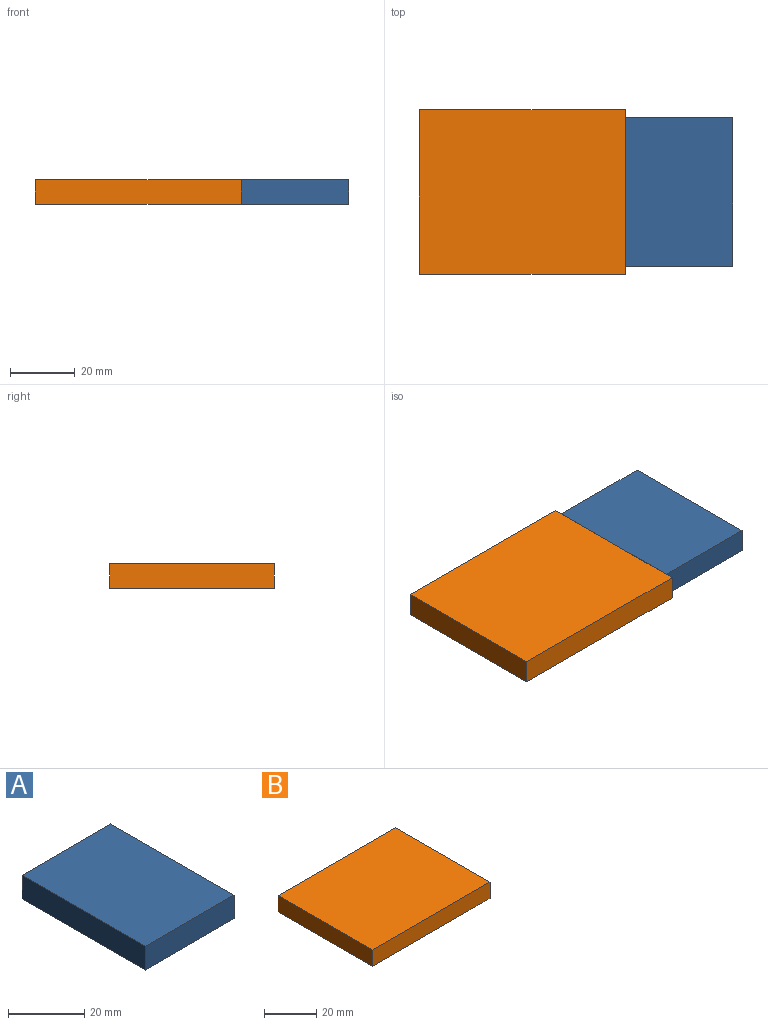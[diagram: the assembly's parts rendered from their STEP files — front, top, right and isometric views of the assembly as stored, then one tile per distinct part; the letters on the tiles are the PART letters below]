
ASSEMBLY  parts=2 mates=1
PART A: 6 faces, bbox 33x45.7x7.6 mm
  f0: plane 45.72x7.62mm, normal (-1,0,0), area 348.4mm2, adj f1,f3,f4,f5
  f1: plane 33.02x7.62mm, normal (0,-1,0), area 251.6mm2, adj f0,f2,f4,f5
  f2: plane 45.72x7.62mm, normal (1,0,0), area 348.4mm2, adj f1,f3,f4,f5
  f3: plane 33.02x7.62mm, normal (0,1,0), area 251.6mm2, adj f0,f2,f4,f5
  f4: plane 45.72x33.02mm, normal (0,0,1), area 1509.7mm2, adj f0,f1,f2,f3
  f5: plane 45.72x33.02mm, normal (0,0,-1), area 1509.7mm2, adj f0,f1,f2,f3
PART B: 6 faces, bbox 63.5x50.8x7.6 mm
  f0: plane 63.5x7.62mm, normal (0,-1,0), area 483.9mm2, adj f1,f3,f4,f5
  f1: plane 50.8x7.62mm, normal (1,0,0), area 387.1mm2, adj f0,f2,f4,f5
  f2: plane 63.5x7.62mm, normal (0,1,0), area 483.9mm2, adj f1,f3,f4,f5
  f3: plane 50.8x7.62mm, normal (-1,0,0), area 387.1mm2, adj f0,f2,f4,f5
  f4: plane 63.5x50.8mm, normal (0,0,1), area 3225.8mm2, adj f0,f1,f2,f3
  f5: plane 63.5x50.8mm, normal (0,0,-1), area 3225.8mm2, adj f0,f1,f2,f3
PLACE A t=(19.24,-4.94,-7.9)mm
PLACE B t=(19.24,-7.48,-7.9)mm
MATE planar B.f1 <-> A.f0  axis (1,0,0) through (19.24,17.92,-4.09)mm
